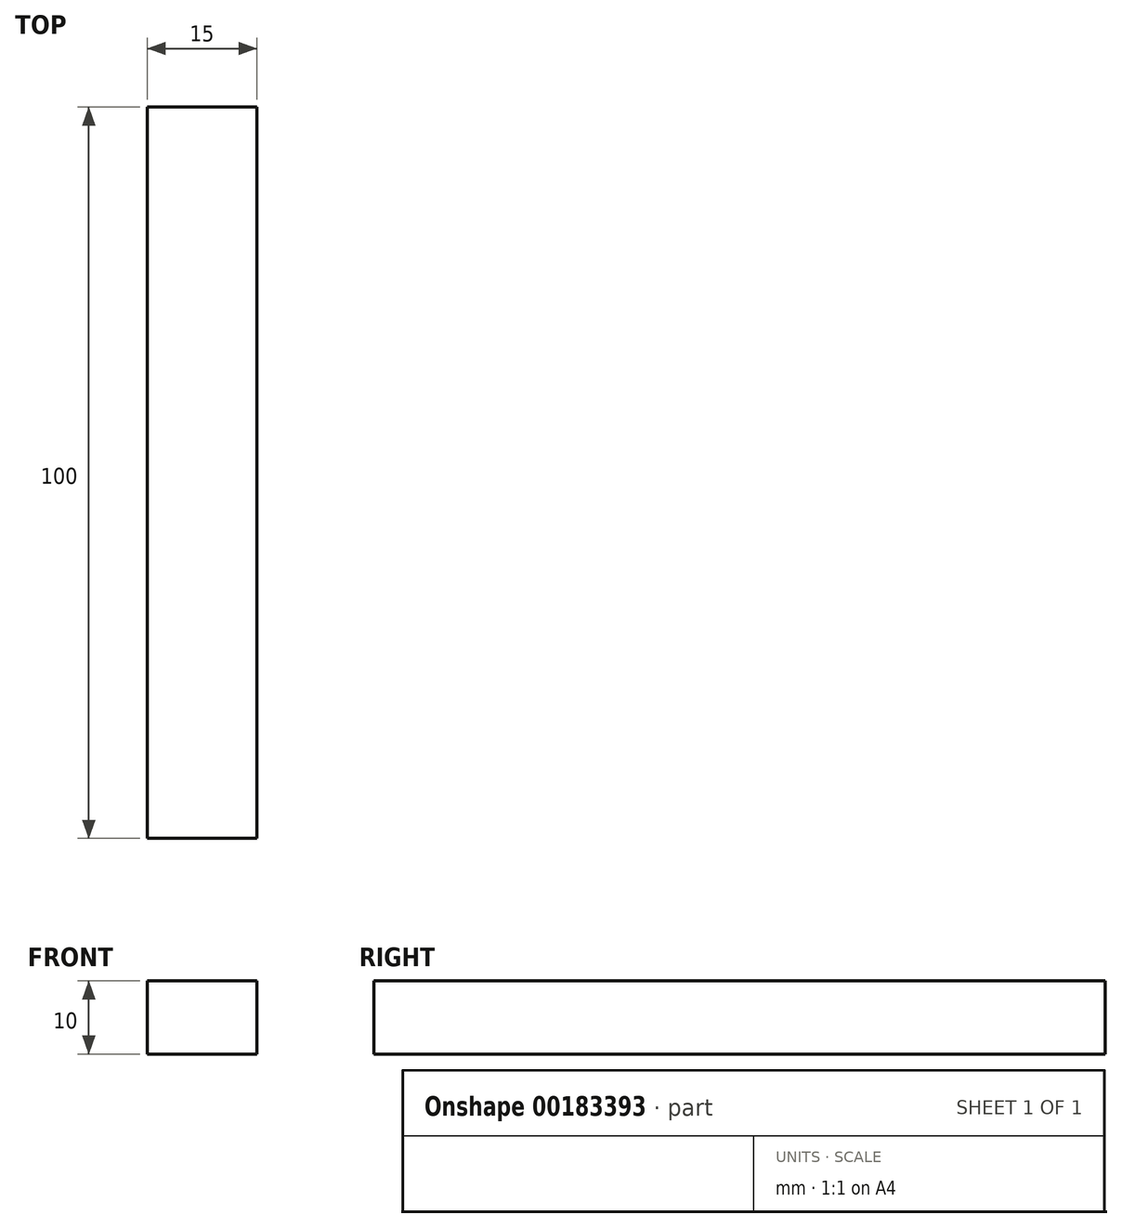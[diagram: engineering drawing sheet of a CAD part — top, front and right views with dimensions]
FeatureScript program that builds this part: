
annotation { "Feature Type Name" : "Feature", "Feature Type Description" : "" }
export const myFeature = defineFeature(function(context is Context, id is Id, definition is map)
    precondition{}
    {
        {
            var Q0;
            Q0=qCreatedBy(makeId("Front.planeOp"),FACE);
            var sketch = newSketch(context, id + "F0", { "sketchPlane" : qUnion([Q0])});
            skLineSegment(sketch, "E0.bottom", {"start": v(0, 0) * mm, "end": v(15, 0) * mm});
            skLineSegment(sketch, "E0.top", {"start": v(0, 10) * mm, "end": v(15, 10) * mm});
            skLineSegment(sketch, "E0.left", {"start": v(0, 0) * mm, "end": v(0, 10) * mm});
            skLineSegment(sketch, "E0.right", {"start": v(15, 0) * mm, "end": v(15, 10) * mm});
            skSolve(sketch);
        }
        {
            var Q0;
            Q0 = qSketchRegion(id + "F0", true);
            extrude(context, id + "F1", {"entities" : qUnion([Q0]), "depth" : 100 * mm});
        }
    });
